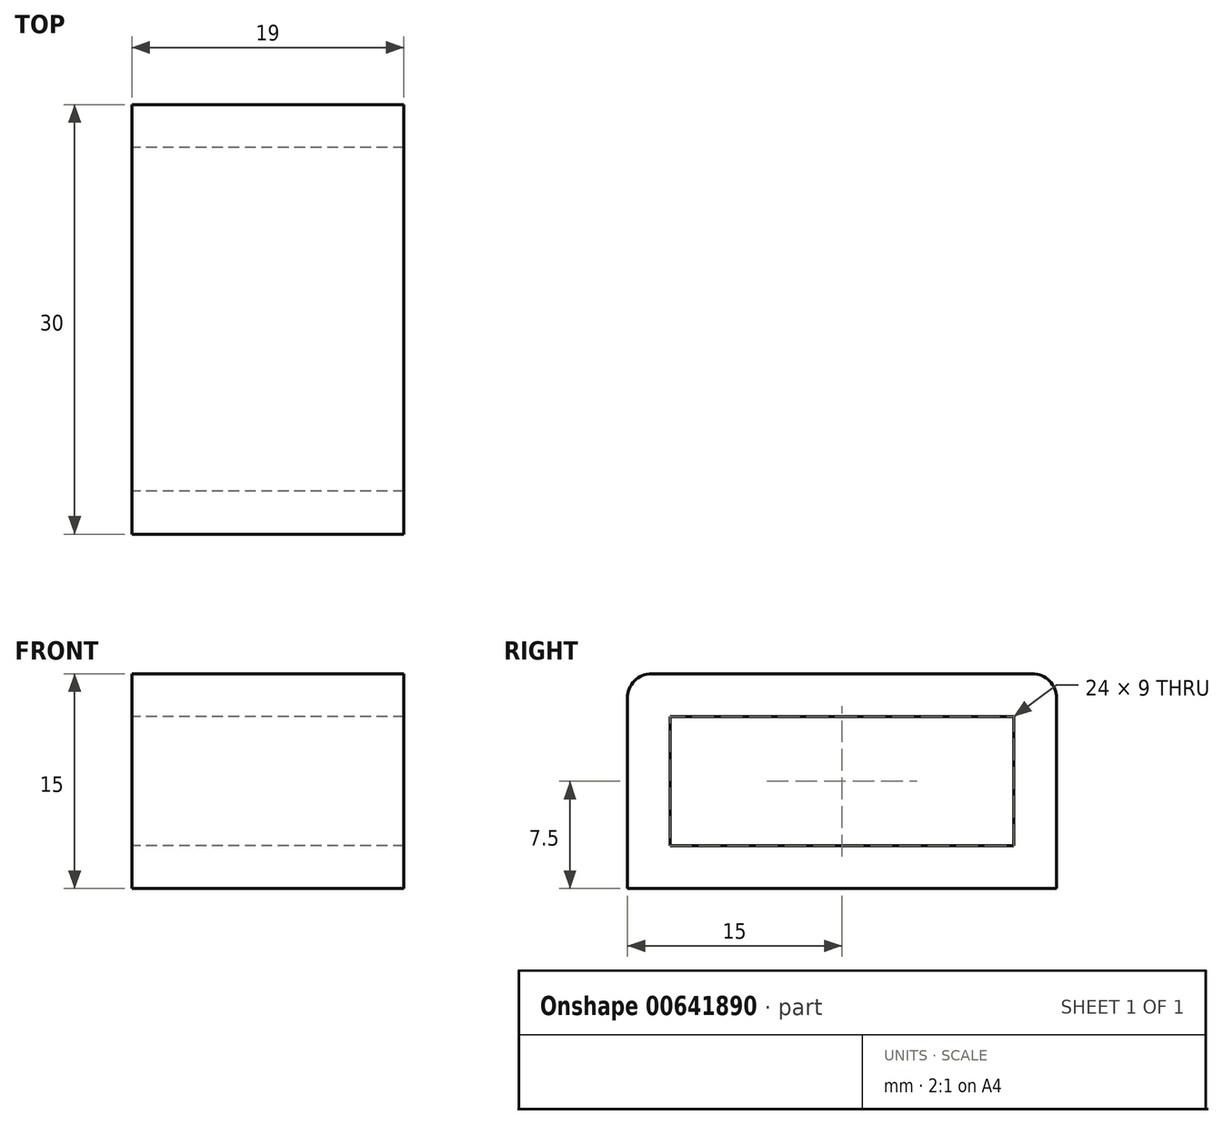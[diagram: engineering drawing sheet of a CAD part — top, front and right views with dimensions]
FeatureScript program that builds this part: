
annotation { "Feature Type Name" : "Feature", "Feature Type Description" : "" }
export const myFeature = defineFeature(function(context is Context, id is Id, definition is map)
    precondition{}
    {
        {
            var Q0;
            Q0=qCreatedBy(makeId("Right.planeOp"),FACE);
            var sketch = newSketch(context, id + "F0", { "sketchPlane" : qUnion([Q0])});
            skLineSegment(sketch, "E0", {"start": v(0, 0) * mm, "end": v(-30, 0) * mm});
            skLineSegment(sketch, "E1", {"start": v(-30, 0) * mm, "end": v(-30, 13.3) * mm});
            skLineSegment(sketch, "E2", {"start": v(-13.86, 15) * mm, "end": v(-1.7, 15) * mm});
            skLineSegment(sketch, "E3", {"start": v(0, 13.3) * mm, "end": v(0, 0) * mm});
            skPoint(sketch, "E4.visualSharp", {"position": v(-30, 15) * mm});
            skLineSegment(sketch, "E5", {"start": v(-13.86, 15) * mm, "end": v(-28.3, 15) * mm});
            skPoint(sketch, "E6.visualSharp", {"position": v(0, 15) * mm});
            skArc(sketch, "E6.filletArc", {"start": v(0, 13.3) * mm, "mid": v(-0.5, 14.5) * mm, "end": v(-1.7, 15) * mm});
            skArc(sketch, "E7.filletArc", {"start": v(-28.3, 15) * mm, "mid": v(-29.5, 14.5) * mm, "end": v(-30, 13.3) * mm});
            skLineSegment(sketch, "E8", {"start": v(-27, 3) * mm, "end": v(-3, 3) * mm});
            skLineSegment(sketch, "E9", {"start": v(-3, 3) * mm, "end": v(-3, 12) * mm});
            skLineSegment(sketch, "E10", {"start": v(-3, 12) * mm, "end": v(-27, 12) * mm});
            skLineSegment(sketch, "E11", {"start": v(-27, 12) * mm, "end": v(-27, 3) * mm});
            skSolve(sketch);
        }
        {
            var Q0;
            Q0=makeQuery(id+"F0.imprint","IMPRINT",FACE,{"disambiguationData":[TD([[makeQuery(id+"F0.imprint","IMPRINT",EDGE,{"derivedFrom":sQuery(id+"F0.wireOp",EDGE,"E0")}),-1.0]])]});
            extrude(context, id + "F1", {"entities" : qUnion([Q0]), "depth" : 19 * mm, "offsetDistance" : 25 * mm});
        }
    });
